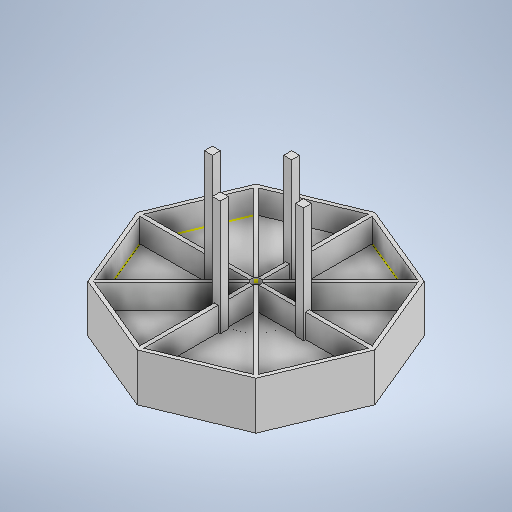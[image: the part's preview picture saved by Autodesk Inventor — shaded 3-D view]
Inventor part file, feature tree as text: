
AUTODESK INVENTOR PART (.ipt)
format: ipt  version: 2025 (Build 290162000, 162)  size: 388,096 bytes
history: native  units: mm
features: sketch x10, extrude x7, projected_geometry x2
ambient origin geometry x8: Origin, YZ Plane, XZ Plane, XY Plane, X Axis, Y Axis, Z Axis, Center Point
bodies: Body1 (feature_tree)
feature tree (19):
  extrude  "Wyciągnięcie proste2"  Depth=300.0mm
  sketch  "Szkic4"
  extrude  "Wyciągnięcie proste3"  Depth=50.0mm TaperAngle=0.0deg
  sketch  "Szkic6"
  extrude  "Wyciągnięcie proste4"  Depth=290.0mm
  extrude  "Wyciągnięcie proste5"  Depth=30.0mm TaperAngle=0.0deg
  extrude  "Wyciągnięcie proste6"  Depth=5.0mm
  sketch  "Szkic10"
  extrude  "Wyciągnięcie proste7"  Depth=5.0mm
  extrude  "Wyciągnięcie proste14"  Depth=5.0mm
  sketch  "Szkic3"
  sketch  "Szkic5"
  sketch  "Szkic7"
  sketch  "Szkic8"
  sketch  "Szkic9"
  sketch  "Szkic11"
  projected_geometry  "Pętla rzutowana1"
  projected_geometry  "Pętla rzutowana2"
  sketch  "Szkic19"
